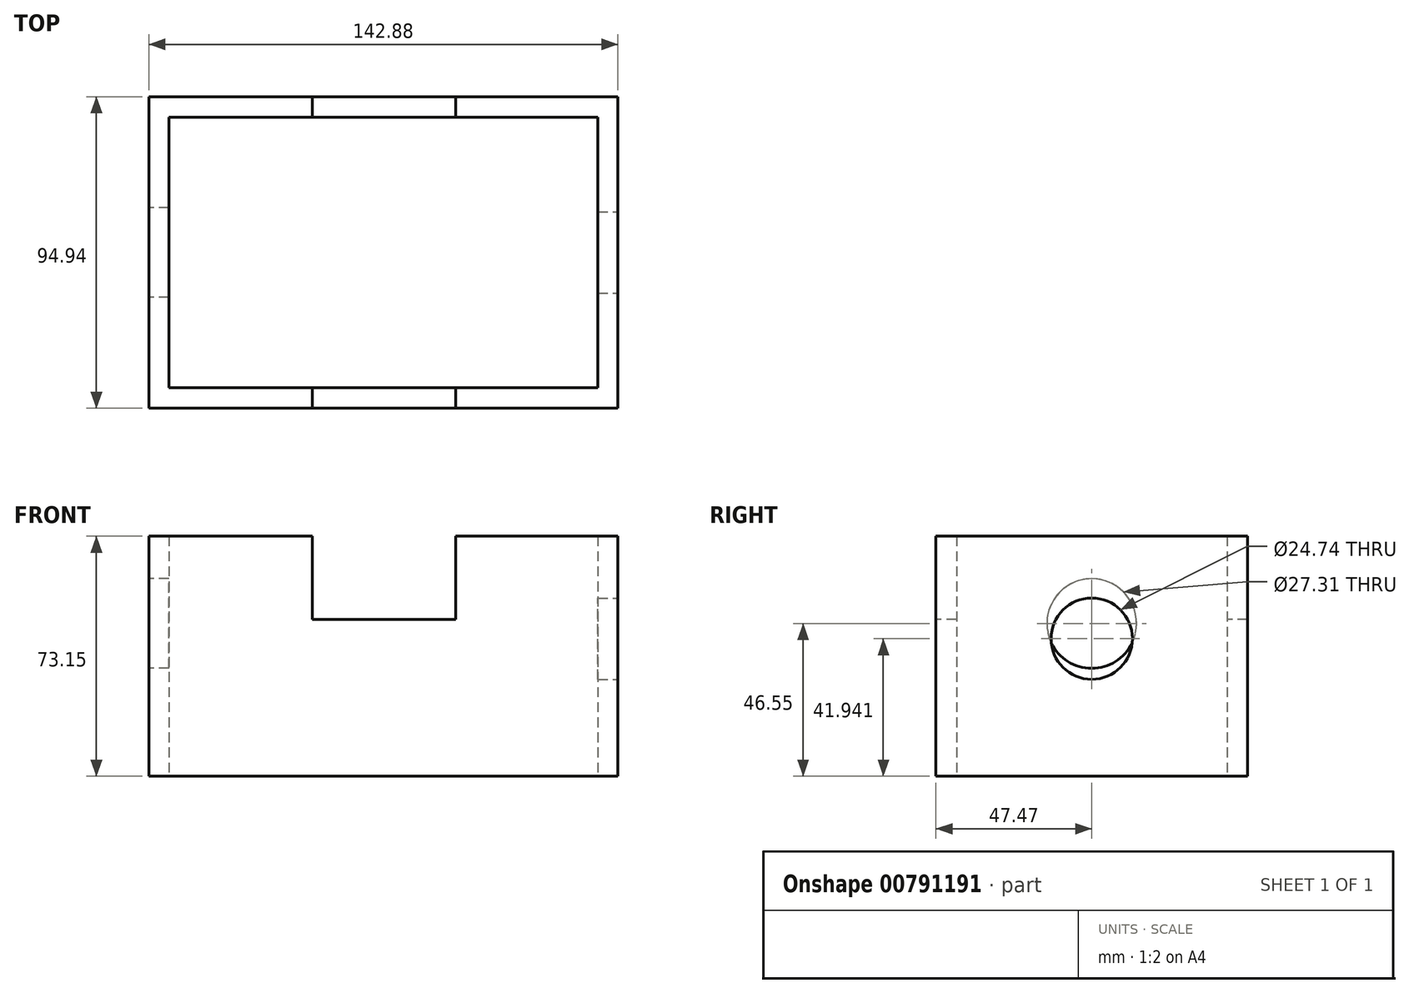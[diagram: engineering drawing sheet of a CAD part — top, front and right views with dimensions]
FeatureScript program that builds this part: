
annotation { "Feature Type Name" : "Feature", "Feature Type Description" : "" }
export const myFeature = defineFeature(function(context is Context, id is Id, definition is map)
    precondition{}
    {
        {
            var Q0;
            Q0=qCreatedBy(makeId("Top.planeOp"),FACE);
            var sketch = newSketch(context, id + "F0", { "sketchPlane" : qUnion([Q0])});
            skLineSegment(sketch, "E0.bottom", {"start": v(-65.35, 41.2) * mm, "end": v(65.35, 41.2) * mm});
            skLineSegment(sketch, "E0.top", {"start": v(-65.35, -41.2) * mm, "end": v(65.35, -41.2) * mm});
            skLineSegment(sketch, "E0.left", {"start": v(-65.35, 41.2) * mm, "end": v(-65.35, -41.2) * mm});
            skLineSegment(sketch, "E0.right", {"start": v(65.35, 41.2) * mm, "end": v(65.35, -41.2) * mm});
            skPoint(sketch, "E0.middle", {"position": v(0, 0) * mm});
            skLineSegment(sketch, "E1.bottom", {"start": v(-71.44, 47.47) * mm, "end": v(71.44, 47.47) * mm});
            skLineSegment(sketch, "E1.top", {"start": v(-71.44, -47.47) * mm, "end": v(71.44, -47.47) * mm});
            skLineSegment(sketch, "E1.left", {"start": v(-71.44, 47.47) * mm, "end": v(-71.44, -47.47) * mm});
            skLineSegment(sketch, "E1.right", {"start": v(71.44, 47.47) * mm, "end": v(71.44, -47.47) * mm});
            skSolve(sketch);
        }
        {
            var Q0;
            Q0=makeQuery(id+"F0.imprint","IMPRINT",FACE,{"disambiguationData":[TD([[makeQuery(id+"F0.imprint","IMPRINT",EDGE,{"derivedFrom":sQuery(id+"F0.wireOp",EDGE,"E0.bottom")}),1.0]])]});
            extrude(context, id + "F1", {"entities" : qUnion([Q0]), "depth" : 47.75 * mm, "offsetDistance" : 25.4 * mm});
        }
        {
            var Q0;
            Q0=makeQuery(id+"F1.opExtrude","CAP_FACE",FACE,{"disambiguationData":[OSD([sQuery(id+"F0.wireOp",EDGE,"E0.bottom"),sQuery(id+"F0.wireOp",EDGE,"E0.top"),sQuery(id+"F0.wireOp",EDGE,"E0.left"),sQuery(id+"F0.wireOp",EDGE,"E0.right"),sQuery(id+"F0.wireOp",EDGE,"E1.bottom"),sQuery(id+"F0.wireOp",EDGE,"E1.top"),sQuery(id+"F0.wireOp",EDGE,"E1.left"),sQuery(id+"F0.wireOp",EDGE,"E1.right")])],"isStart":false});
            var sketch = newSketch(context, id + "F2", { "sketchPlane" : qUnion([Q0])});
            skLineSegment(sketch, "E2.bottom", {"start": v(71.44, 47.47) * mm, "end": v(22, 47.47) * mm});
            skLineSegment(sketch, "E2.top", {"start": v(71.44, -47.47) * mm, "end": v(22, -47.47) * mm});
            skLineSegment(sketch, "E2.left", {"start": v(71.44, 47.47) * mm, "end": v(71.44, -47.47) * mm});
            skLineSegment(sketch, "E2.right", {"start": v(22, 47.47) * mm, "end": v(22, -47.47) * mm});
            skSolve(sketch);
        }
        {
            var Q0;
            {var subQ1=sQuery(id+"F2.wireOp",EDGE,"E2.bottom");Q0=makeQuery(id+"F2.imprint","IMPRINT",FACE,{"disambiguationData":[TD([[makeQuery(id+"F2.imprint","IMPRINT",EDGE,{"derivedFrom":subQ1}),-1.0]])]});}
            extrude(context, id + "F3", {"entities" : qUnion([Q0]), "operationType" : NewBodyOperationType.ADD, "depth" : 25.4 * mm, "offsetDistance" : 25.4 * mm});
        }
        {
            var Q0;
            Q0=makeQuery(id+"F1.opExtrude","CAP_FACE",FACE,{"disambiguationData":[OSD([sQuery(id+"F0.wireOp",EDGE,"E0.bottom"),sQuery(id+"F0.wireOp",EDGE,"E0.top"),sQuery(id+"F0.wireOp",EDGE,"E0.left"),sQuery(id+"F0.wireOp",EDGE,"E0.right"),sQuery(id+"F0.wireOp",EDGE,"E1.bottom"),sQuery(id+"F0.wireOp",EDGE,"E1.top"),sQuery(id+"F0.wireOp",EDGE,"E1.left"),sQuery(id+"F0.wireOp",EDGE,"E1.right")])],"isStart":false});
            var sketch = newSketch(context, id + "F4", { "sketchPlane" : qUnion([Q0])});
            skPoint(sketch, "E3.oppositeSnap0", {"position": v(-21.68, -41.2) * mm});
            skLineSegment(sketch, "E3.bottom", {"start": v(-71.44, 47.47) * mm, "end": v(-21.68, 47.47) * mm});
            skLineSegment(sketch, "E3.top", {"start": v(-71.44, -47.47) * mm, "end": v(-21.68, -47.47) * mm});
            skLineSegment(sketch, "E3.left", {"start": v(-71.44, 47.47) * mm, "end": v(-71.44, -47.47) * mm});
            skLineSegment(sketch, "E3.right", {"start": v(-21.68, 47.47) * mm, "end": v(-21.68, -47.47) * mm});
            skSolve(sketch);
        }
        {
            var Q0;
            {var subQ1=sQuery(id+"F4.wireOp",EDGE,"E3.bottom");Q0=makeQuery(id+"F4.imprint","IMPRINT",FACE,{"disambiguationData":[TD([[makeQuery(id+"F4.imprint","IMPRINT",EDGE,{"derivedFrom":subQ1}),-1.0]])]});}
            extrude(context, id + "F5", {"entities" : qUnion([Q0]), "operationType" : NewBodyOperationType.ADD, "depth" : 25.4 * mm, "offsetDistance" : 25.4 * mm});
        }
        {
            var Q0;
            Q0=makeQuery(id+"F3.boolean.opBoolean","MERGE",FACE,{"derivedFrom":[makeQuery(id+"F1.opExtrude","SWEPT_FACE",FACE,{"disambiguationData":[OSD([sQuery(id+"F0.wireOp",EDGE,"E1.right")])]}),makeQuery(id+"F3.opExtrude","SWEPT_FACE",FACE,{"disambiguationData":[OSD([sQuery(id+"F2.wireOp",EDGE,"E2.left")])]})]});
            var sketch = newSketch(context, id + "F6", { "sketchPlane" : qUnion([Q0])});
            skSolve(sketch);
        }
        {
            var Q0;
            {var subQ0=sQuery(id+"F0.wireOp",EDGE,"E1.right");Q0=makeQuery(id+"F6.imprint","IMPRINT",FACE,{"disambiguationData":[TD([[makeQuery(id+"F6.imprint","IMPRINT",EDGE,{"derivedFrom":makeQuery(id+"F1.opExtrude","CAP_EDGE",EDGE,{"disambiguationData":[OSD([subQ0])],"isStart":true})}),-1.0]])]});}
            var sketch = newSketch(context, id + "F7", { "sketchPlane" : qUnion([Q0])});
            skCircle(sketch, "E4", {"center": v(0, 41.94) * mm, "radius": 12.37 * mm});
            skSolve(sketch);
        }
        {
            var Q0;
            Q0=makeQuery(id+"F7.imprint","IMPRINT",FACE,{"disambiguationData":[TD([[makeQuery(id+"F7.imprint","IMPRINT",EDGE,{"derivedFrom":sQuery(id+"F7.wireOp",EDGE,"E4")}),1.0]])]});
            extrude(context, id + "F8", {"entities" : qUnion([Q0]), "operationType" : NewBodyOperationType.REMOVE, "oppositeDirection" : true, "depth" : 25.4 * mm, "offsetDistance" : 25.4 * mm});
        }
        {
            var Q0;
            Q0=makeQuery(id+"F5.boolean.opBoolean","MERGE",FACE,{"derivedFrom":[makeQuery(id+"F1.opExtrude","SWEPT_FACE",FACE,{"disambiguationData":[OSD([sQuery(id+"F0.wireOp",EDGE,"E1.left")])]}),makeQuery(id+"F5.opExtrude","SWEPT_FACE",FACE,{"disambiguationData":[OSD([sQuery(id+"F4.wireOp",EDGE,"E3.left")])]})]});
            var sketch = newSketch(context, id + "F9", { "sketchPlane" : qUnion([Q0])});
            skCircle(sketch, "E5", {"center": v(0, 46.55) * mm, "radius": 13.65 * mm});
            skSolve(sketch);
        }
        {
            var Q0;
            Q0=makeQuery(id+"F9.imprint","IMPRINT",FACE,{"disambiguationData":[TD([[makeQuery(id+"F9.imprint","IMPRINT",EDGE,{"derivedFrom":sQuery(id+"F9.wireOp",EDGE,"E5")}),1.0]])]});
            extrude(context, id + "F10", {"entities" : qUnion([Q0]), "operationType" : NewBodyOperationType.REMOVE, "oppositeDirection" : true, "depth" : 25.4 * mm, "offsetDistance" : 25.4 * mm});
        }
    });
